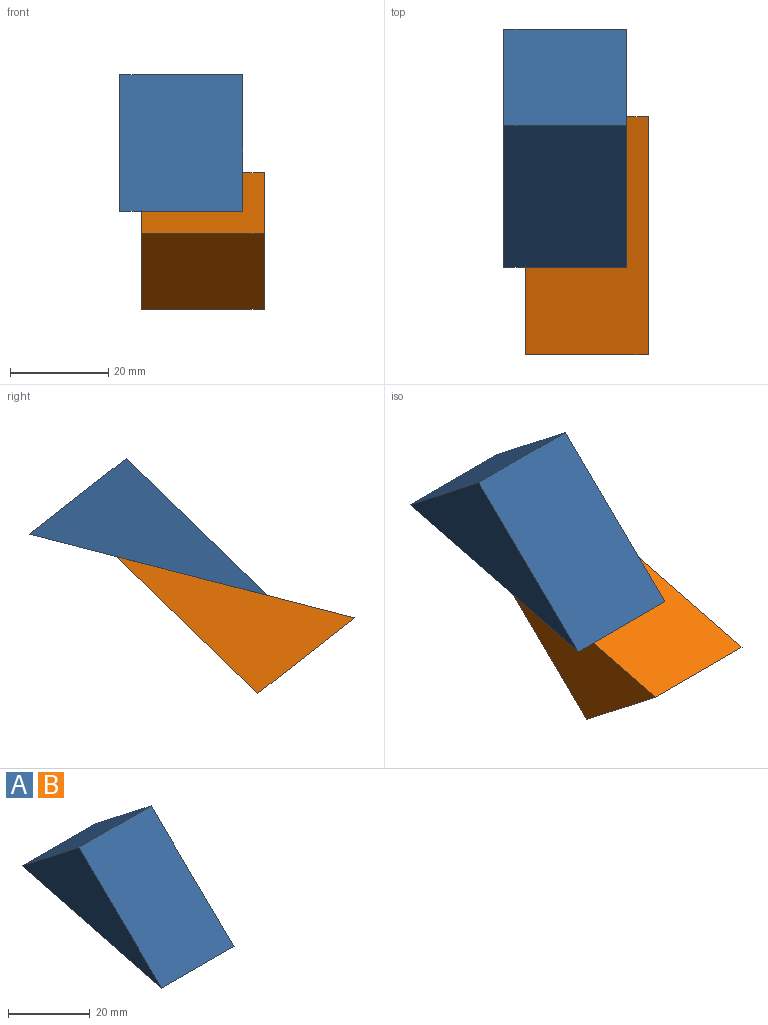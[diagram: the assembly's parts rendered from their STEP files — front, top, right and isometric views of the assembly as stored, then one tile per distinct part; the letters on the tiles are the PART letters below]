
ASSEMBLY  parts=2 mates=1
PART A: 5 faces, bbox 25x48.4x27.8 mm
  f0: plane 25x19.71mm, normal (0,0.62,0.79), area 625mm2, adj f1,f2,f3,f4
  f1: plane 28.71x27.85mm, normal (0,-0.7,0.72), area 1000mm2, adj f0,f2,f3,f4
  f2: plane 48.42x25mm, normal (0,0.25,-0.97), area 1250mm2, adj f0,f1,f3,f4
  f3: plane 48.42x27.85mm, normal (1,0,0), area 495.3mm2, adj f0,f1,f2
  f4: plane 48.42x27.85mm, normal (-1,0,0), area 495.3mm2, adj f0,f1,f2
PART B: same geometry as A
PLACE A t=(-15.21,13.45,-24.65)mm
PLACE B rot(axis=(1,0,0),180deg) t=(-10.86,44.04,10.87)mm
MATE planar B.f2 <-> A.f2  axis (0,-0.25,0.97) through (1.64,19.83,-9.19)mm
